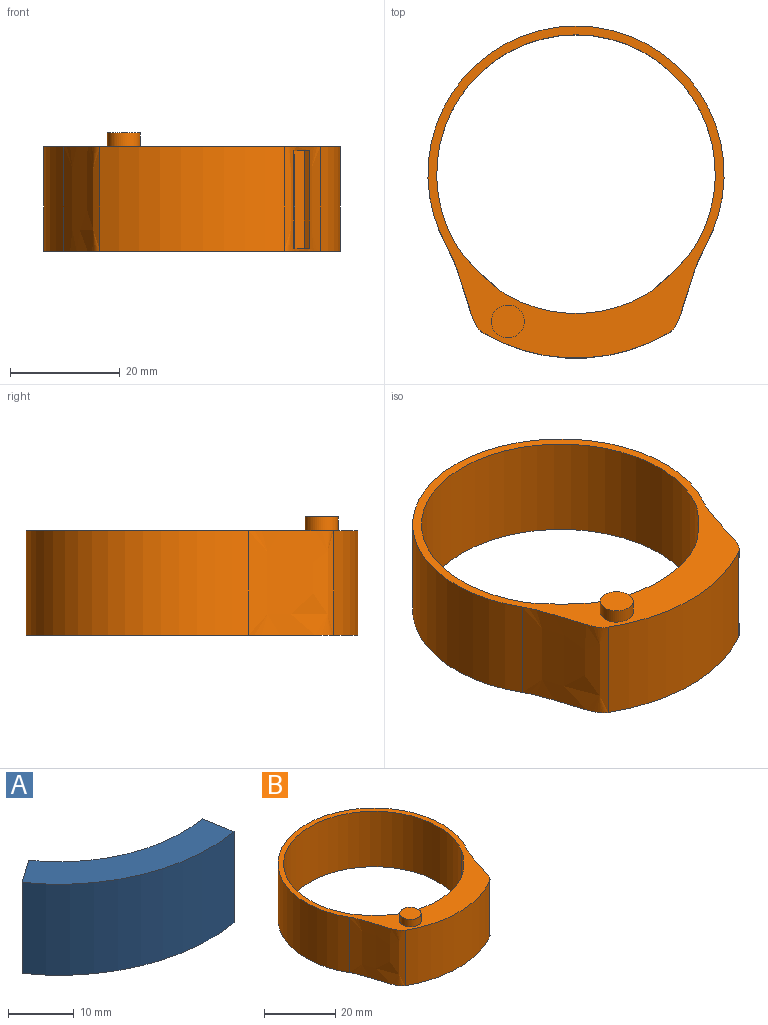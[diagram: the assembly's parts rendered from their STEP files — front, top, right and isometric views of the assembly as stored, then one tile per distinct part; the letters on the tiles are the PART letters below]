
ASSEMBLY  parts=2 mates=1
PART A: 6 faces, bbox 32.4x17.3x17 mm
  f0: cylinder r=26.67mm len=26.48mm, axis (0,0,-1), area 514.9mm2, adj f1,f3,f4,f5
  f1: plane 32.35x17.29mm, normal (0,0,1), area 198.9mm2, adj f0,f2,f4,f5
  f2: cylinder r=32.59mm len=32.35mm, axis (0,0,-1), area 629.2mm2, adj f1,f3,f4,f5
  f3: plane 32.35x17.29mm, normal (0,0,-1), area 198.9mm2, adj f0,f2,f4,f5
  f4: plane 17.02x5.83mm, normal (0.98,0.17,0), area 100.7mm2, adj f0,f1,f2,f3
  f5: plane 17.02x4.85mm, normal (-0.57,0.82,0), area 100.7mm2, adj f0,f1,f2,f3
PART B: 18 faces, bbox 54x60.6x21.6 mm
  f0: plane 60.56x54.02mm, normal (0,0,1), area 529.4mm2, adj f1,f3,f4,f5,f6,f7,f8,f9
  f1: cylinder r=25.4mm len=50.8mm, axis (0,0,-1), area 2026.8mm2, adj f0,f2,f7,f8
  f2: plane 60.56x54.02mm, normal (0,0,-1), area 557.6mm2, adj f1,f3,f4,f5,f6,f7,f8,f9
  f3: cylinder r=27.01mm len=54.02mm, axis (0,0,-1), area 2155.2mm2, adj f0,f2,f6,f9
  f4: cylinder r=25.4mm len=25.4mm, axis (0,0,-1), area 506.7mm2, adj f0,f2,f7,f8
  f5: cylinder r=33.55mm len=33.55mm, axis (0,0,-1), area 669.3mm2, adj f0,f2,f6,f9
  f6: bspline ~19.05x15.55mm, area 326.1mm2, adj f0,f2,f3,f5
  f7: bspline ~19.05x9.3mm, area 252.2mm2, adj f0,f1,f2,f4
  f8: bspline ~19.05x9.3mm, area 252.2mm2, adj f0,f1,f2,f4
  f9: bspline ~19.05x15.55mm, area 160.8mm2, adj f0,f2,f3,f5,f11,f12,f13,f15
  f10: cylinder r=26.67mm len=31.7mm, axis (0,0,1), area 620.7mm2, adj f11,f13,f14,f15
  f11: plane 35.26x15.5mm, normal (0,0,-1), area 210.6mm2, adj f9,f10,f12,f14,f15
  f12: cylinder r=32.64mm len=32.37mm, axis (0,0,1), area 604.5mm2, adj f9,f11,f13,f14
  f13: plane 35.26x15.5mm, normal (0,0,1), area 210.6mm2, adj f9,f10,f12,f14,f15
  f14: plane 17.78x5.41mm, normal (0.91,-0.42,0), area 106.1mm2, adj f10,f11,f12,f13
  f15: plane 17.78x1.04mm, normal (-0.64,-0.77,0), area 24mm2, adj f9,f10,f11,f13
  f16: cylinder r=3mm len=6mm, axis (0,0,-1), area 47.9mm2, adj f0,f17
  f17: plane 6x6mm, normal (0,0,1), area 28.3mm2, adj f16
PLACE A rot(axis=(0,0,1),25deg) t=(-2.35,0.65,-9.2)mm
PLACE B t=(-2.35,0.65,-9.76)mm fixed
MATE revolute A.f0 <-> B.f1  axis (0,0,-1) through (-2.35,0.65,-9.2)mm
